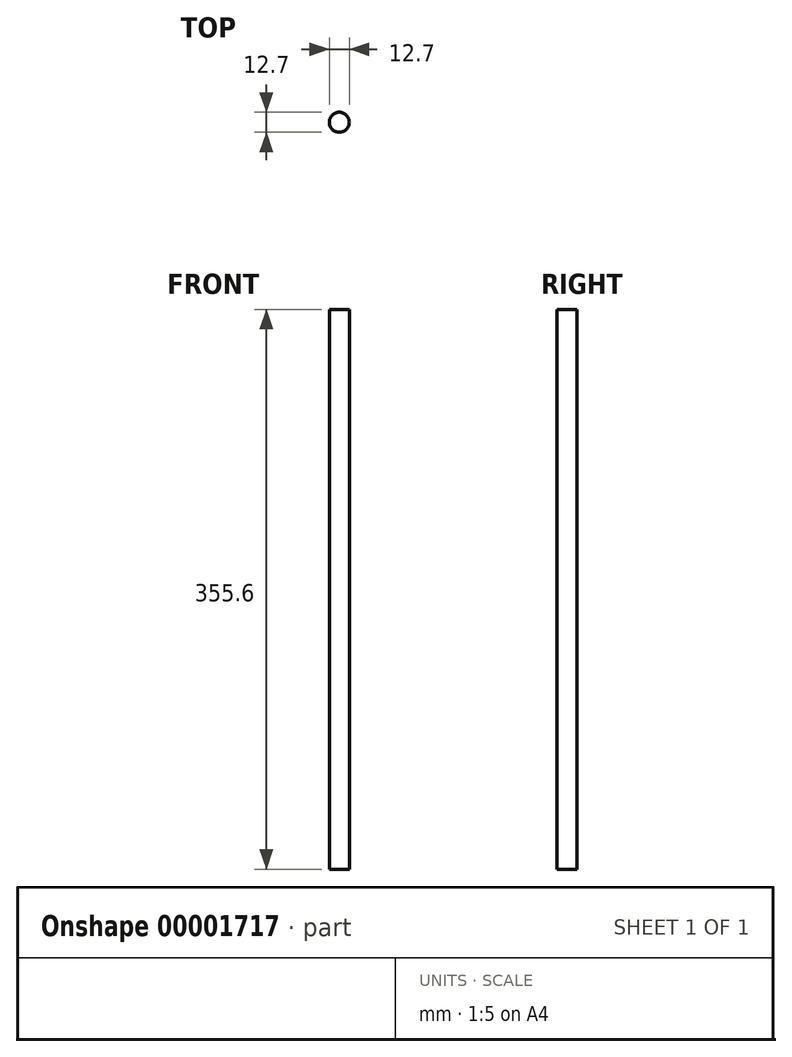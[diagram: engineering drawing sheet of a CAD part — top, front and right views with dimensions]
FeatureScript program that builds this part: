
annotation { "Feature Type Name" : "Feature", "Feature Type Description" : "" }
export const myFeature = defineFeature(function(context is Context, id is Id, definition is map)
    precondition{}
    {
        {
            var Q0;
            Q0=qCreatedBy(makeId("Top.planeOp"),FACE);
            var sketch = newSketch(context, id + "F0", { "sketchPlane" : qUnion([Q0])});
            skCircle(sketch, "E0", {"center": v(0, 0) * mm, "radius": 6.35 * mm});
            skSolve(sketch);
        }
        {
            var Q0;
            Q0 = qSketchRegion(id + "F0", true);
            extrude(context, id + "F1", {"entities" : qUnion([Q0]), "depth" : 355.6 * mm});
        }
    });
